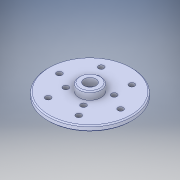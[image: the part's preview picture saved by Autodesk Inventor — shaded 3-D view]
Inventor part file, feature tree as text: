
AUTODESK INVENTOR PART (.ipt)
format: ipt  version: 2018 (Build 220112000, 112)  size: 153,088 bytes
history: native  units: in
note: dims shown in document units (in); Inventor stores cm internally (conversion verified against a paired STEP export)
features: chamfer x1
ambient origin geometry x8: Origin, YZ Plane, XZ Plane, XY Plane, X Axis, Y Axis, Z Axis, Center Point
bodies: Solid1 (feature_tree)
feature tree (1):
  chamfer  "Chamfer1"  [1 undecoded]
note: 1 required parameter value undecoded (feature->parameter linkage not recoverable at this tier; creation-order binding heuristic only, values carry confidence <= 0.55)
